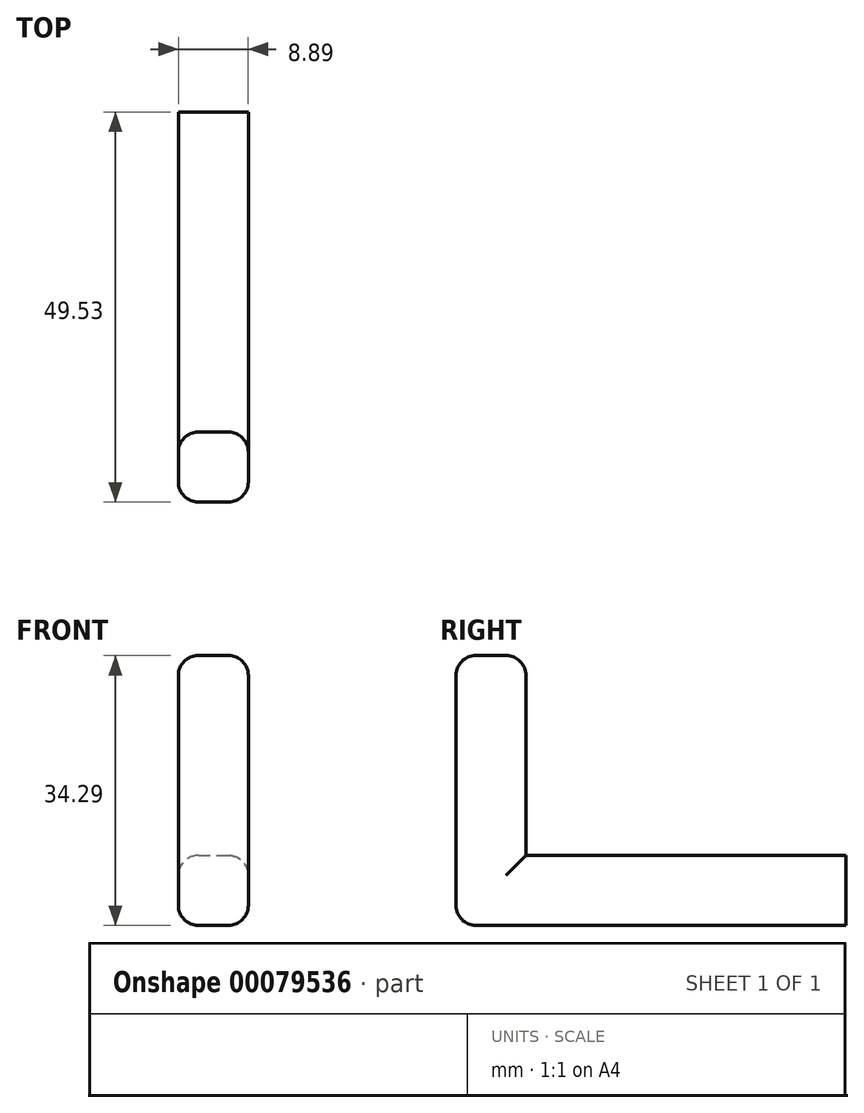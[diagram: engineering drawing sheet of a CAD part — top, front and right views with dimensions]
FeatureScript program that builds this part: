
annotation { "Feature Type Name" : "Feature", "Feature Type Description" : "" }
export const myFeature = defineFeature(function(context is Context, id is Id, definition is map)
    precondition{}
    {
        {
            var Q0;
            Q0=qCreatedBy(makeId("Front.planeOp"),FACE);
            var sketch = newSketch(context, id + "F0", { "sketchPlane" : qUnion([Q0])});
            skLineSegment(sketch, "E0.bottom", {"start": v(-3.72, 4.78) * mm, "end": v(5.17, 4.78) * mm});
            skLineSegment(sketch, "E0.top", {"start": v(-3.72, -4.1) * mm, "end": v(5.17, -4.1) * mm});
            skLineSegment(sketch, "E0.left", {"start": v(-3.72, 4.78) * mm, "end": v(-3.72, -4.1) * mm});
            skLineSegment(sketch, "E0.right", {"start": v(5.17, 4.78) * mm, "end": v(5.17, -4.1) * mm});
            skSolve(sketch);
        }
        {
            var Q0;
            Q0 = qSketchRegion(id + "F0", true);
            extrude(context, id + "F1", {"entities" : qUnion([Q0]), "depth" : 40.64 * mm});
        }
        {
            var Q0;
            Q0=makeQuery(id+"F1.opExtrude","CAP_FACE",FACE,{"disambiguationData":[OSD([sQuery(id+"F0.wireOp",EDGE,"E0.bottom"),sQuery(id+"F0.wireOp",EDGE,"E0.top"),sQuery(id+"F0.wireOp",EDGE,"E0.left"),sQuery(id+"F0.wireOp",EDGE,"E0.right")])],"isStart":false});
            var sketch = newSketch(context, id + "F2", { "sketchPlane" : qUnion([Q0])});
            skLineSegment(sketch, "E1.bottom", {"start": v(-3.72, -4.1) * mm, "end": v(5.17, -4.1) * mm});
            skLineSegment(sketch, "E1.top", {"start": v(-3.72, 30.18) * mm, "end": v(5.17, 30.18) * mm});
            skLineSegment(sketch, "E1.left", {"start": v(-3.72, -4.1) * mm, "end": v(-3.72, 30.18) * mm});
            skLineSegment(sketch, "E1.right", {"start": v(5.17, -4.1) * mm, "end": v(5.17, 30.18) * mm});
            skSolve(sketch);
        }
        {
            var Q0;
            Q0 = qSketchRegion(id + "F2", true);
            extrude(context, id + "F3", {"entities" : qUnion([Q0]), "operationType" : NewBodyOperationType.ADD, "depth" : 8.9 * mm});
        }
        {
            var Q0;
            Q0=makeQuery(id+"F3.opExtrude","CAP_EDGE",EDGE,{"disambiguationData":[OSD([sQuery(id+"F2.wireOp",EDGE,"E1.right")])],"isStart":true});
            var Q1;
            Q1=makeQuery(id+"F3.opExtrude","CAP_EDGE",EDGE,{"disambiguationData":[OSD([sQuery(id+"F2.wireOp",EDGE,"E1.top")])],"isStart":true});
            var Q2;
            Q2=makeQuery(id+"F3.opExtrude","CAP_EDGE",EDGE,{"disambiguationData":[OSD([sQuery(id+"F2.wireOp",EDGE,"E1.left")])],"isStart":true});
            var Q3;
            Q3=makeQuery(id+"F3.opExtrude","SWEPT_EDGE",EDGE,{"disambiguationData":[OSD([sQuery(id+"F2.wireOp",EDGE,"E1.top"),sQuery(id+"F2.wireOp",EDGE,"E1.left")])]});
            var Q4;
            Q4=makeQuery(id+"F3.opExtrude","CAP_EDGE",EDGE,{"disambiguationData":[OSD([sQuery(id+"F2.wireOp",EDGE,"E1.left")])],"isStart":false});
            var Q5;
            Q5=makeQuery(id+"F1.opExtrude","SWEPT_EDGE",EDGE,{"disambiguationData":[OSD([sQuery(id+"F0.wireOp",EDGE,"E0.bottom"),sQuery(id+"F0.wireOp",EDGE,"E0.left")])]});
            var Q6;
            Q6=makeQuery(id+"F3.boolean.opBoolean","MERGE",EDGE,{"derivedFrom":[makeQuery(id+"F1.opExtrude","SWEPT_EDGE",EDGE,{"disambiguationData":[OSD([sQuery(id+"F0.wireOp",EDGE,"E0.top"),sQuery(id+"F0.wireOp",EDGE,"E0.left")])]}),makeQuery(id+"F3.opExtrude","SWEPT_EDGE",EDGE,{"disambiguationData":[OSD([sQuery(id+"F2.wireOp",EDGE,"E1.bottom"),sQuery(id+"F2.wireOp",EDGE,"E1.left")])]})]});
            var Q7;
            Q7=makeQuery(id+"F1.opExtrude","SWEPT_EDGE",EDGE,{"disambiguationData":[OSD([sQuery(id+"F0.wireOp",EDGE,"E0.bottom"),sQuery(id+"F0.wireOp",EDGE,"E0.right")])]});
            var Q8;
            Q8=makeQuery(id+"F3.opExtrude","CAP_EDGE",EDGE,{"disambiguationData":[OSD([sQuery(id+"F2.wireOp",EDGE,"E1.right")])],"isStart":false});
            var Q9;
            Q9=makeQuery(id+"F3.boolean.opBoolean","MERGE",EDGE,{"derivedFrom":[makeQuery(id+"F1.opExtrude","SWEPT_EDGE",EDGE,{"disambiguationData":[OSD([sQuery(id+"F0.wireOp",EDGE,"E0.top"),sQuery(id+"F0.wireOp",EDGE,"E0.right")])]}),makeQuery(id+"F3.opExtrude","SWEPT_EDGE",EDGE,{"disambiguationData":[OSD([sQuery(id+"F2.wireOp",EDGE,"E1.bottom"),sQuery(id+"F2.wireOp",EDGE,"E1.right")])]})]});
            var Q10;
            Q10=makeQuery(id+"F3.opExtrude","CAP_EDGE",EDGE,{"disambiguationData":[OSD([sQuery(id+"F2.wireOp",EDGE,"E1.bottom")])],"isStart":false});
            var Q11;
            Q11=makeQuery(id+"F3.opExtrude","SWEPT_EDGE",EDGE,{"disambiguationData":[OSD([sQuery(id+"F2.wireOp",EDGE,"E1.top"),sQuery(id+"F2.wireOp",EDGE,"E1.right")])]});
            var Q12;
            Q12=makeQuery(id+"F3.opExtrude","CAP_EDGE",EDGE,{"disambiguationData":[OSD([sQuery(id+"F2.wireOp",EDGE,"E1.top")])],"isStart":false});
            fillet(context, id + "F4", {"entities" : qUnion([Q0, Q1, Q2, Q3, Q4, Q5, Q6, Q7, Q8, Q9, Q10, Q11, Q12]), "radius" : 2.54 * mm, "tangentPropagation" : true, "allowEdgeOverflow" : false});
        }
    });
